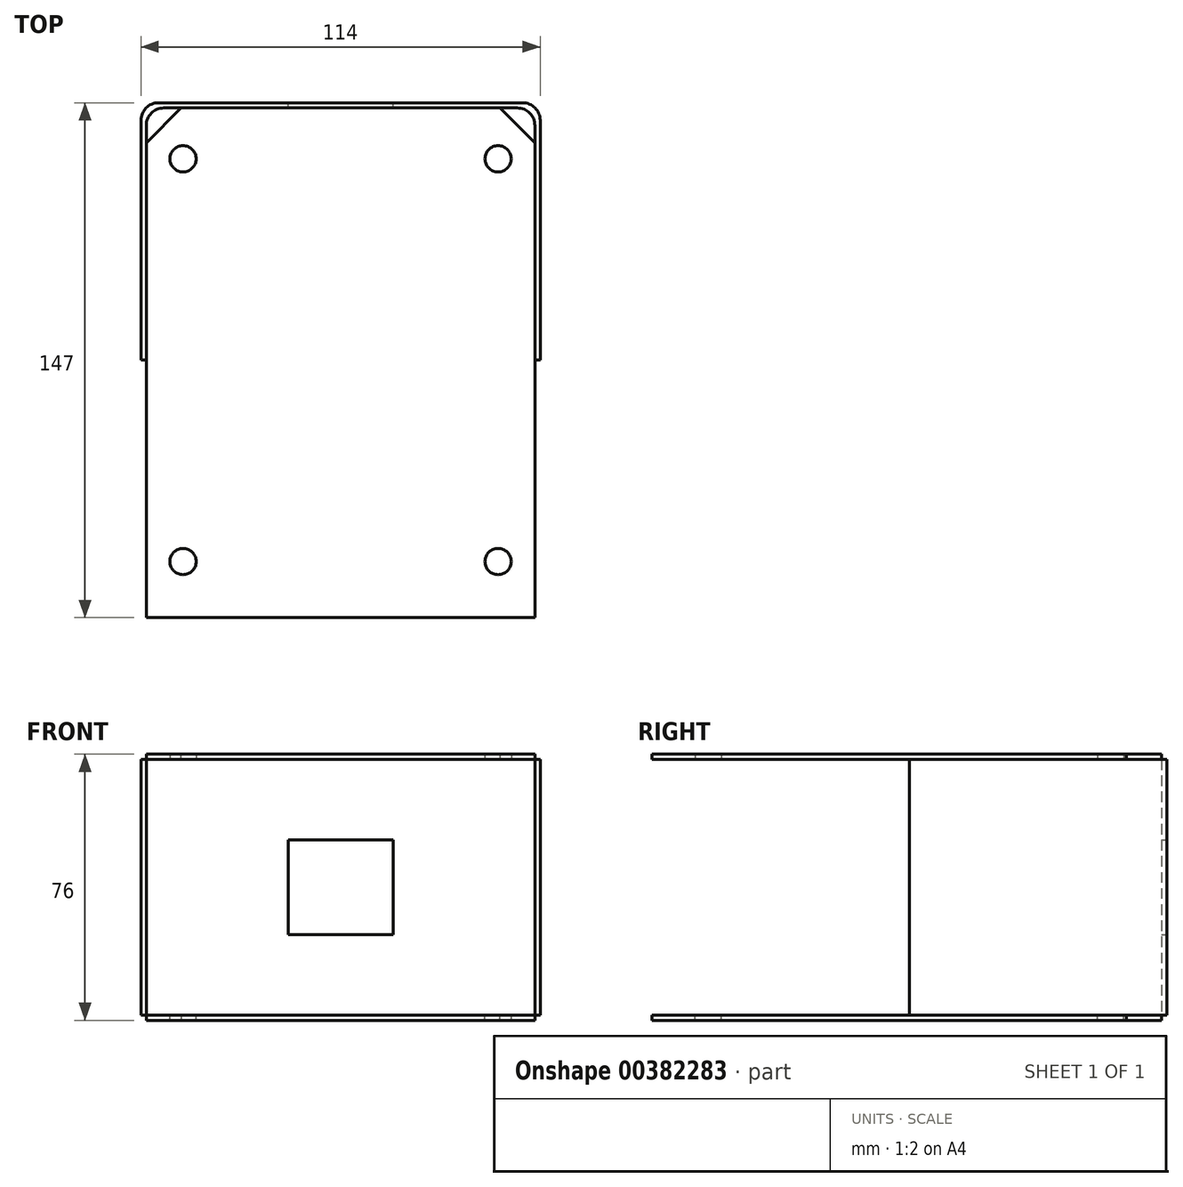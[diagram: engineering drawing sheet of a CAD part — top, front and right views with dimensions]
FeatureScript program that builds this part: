
annotation { "Feature Type Name" : "Feature", "Feature Type Description" : "" }
export const myFeature = defineFeature(function(context is Context, id is Id, definition is map)
    precondition{}
    {
        {
            var Q0;
            Q0=qCreatedBy(makeId("Top.planeOp"),FACE);
            var sketch = newSketch(context, id + "F0", { "sketchPlane" : qUnion([Q0])});
            skLineSegment(sketch, "E0.bottom", {"start": v(57, -73.5) * mm, "end": v(-57, -73.5) * mm});
            skLineSegment(sketch, "E0.top", {"start": v(57, 73.5) * mm, "end": v(-57, 73.5) * mm});
            skLineSegment(sketch, "E0.left", {"start": v(57, -73.5) * mm, "end": v(57, 73.5) * mm});
            skLineSegment(sketch, "E0.right", {"start": v(-57, -73.5) * mm, "end": v(-57, 73.5) * mm});
            skPoint(sketch, "E0.middle", {"position": v(0, 0) * mm});
            skLineSegment(sketch, "E1.0", {"start": v(55.5, -73.5) * mm, "end": v(55.5, 72) * mm});
            skLineSegment(sketch, "E1.1", {"start": v(55.5, 72) * mm, "end": v(-55.5, 72) * mm});
            skLineSegment(sketch, "E1.2", {"start": v(-55.5, -73.5) * mm, "end": v(-55.5, 72) * mm});
            skLineSegment(sketch, "E2.bottom", {"start": v(-57, -73.5) * mm, "end": v(57, -73.5) * mm});
            skLineSegment(sketch, "E2.top", {"start": v(-57, 0) * mm, "end": v(57, 0) * mm});
            skLineSegment(sketch, "E2.left", {"start": v(-57, -73.5) * mm, "end": v(-57, 0) * mm});
            skLineSegment(sketch, "E2.right", {"start": v(57, -73.5) * mm, "end": v(57, 0) * mm});
            skLineSegment(sketch, "E3.top", {"start": v(-57, -36.75) * mm, "end": v(57, -36.75) * mm});
            skLineSegment(sketch, "E3.left", {"start": v(-57, -73.5) * mm, "end": v(-57, -36.75) * mm});
            skLineSegment(sketch, "E3.right", {"start": v(57, -73.5) * mm, "end": v(57, -36.75) * mm});
            skSolve(sketch);
        }
        {
            var Q0;
            {var subQ5=sQuery(id+"F0.wireOp",EDGE,"E2.left");Q0=makeQuery(id+"F0.imprint","IMPRINT",FACE,{"disambiguationData":[TD([[makeQuery(id+"F0.imprint","IMPRINT",EDGE,{"derivedFrom":subQ5}),-1.0]])]});}
            var Q1;
            {var subQ5=sQuery(id+"F0.wireOp",EDGE,"E2.right");Q1=makeQuery(id+"F0.imprint","IMPRINT",FACE,{"disambiguationData":[TD([[makeQuery(id+"F0.imprint","IMPRINT",EDGE,{"derivedFrom":subQ5}),1.0]])]});}
            var Q2;
            Q2=makeQuery(id+"F0.imprint","IMPRINT",FACE,{"disambiguationData":[TD([[makeQuery(id+"F0.imprint","IMPRINT",EDGE,{"derivedFrom":sQuery(id+"F0.wireOp",EDGE,"E0.top")}),1.0]])]});
            extrude(context, id + "F1", {"entities" : qUnion([Q0, Q1, Q2]), "endBound" : BoundingType.SYMMETRIC, "depth" : 73 * mm});
        }
        {
            var Q0;
            Q0=makeQuery(id+"F1.opExtrude","SWEPT_EDGE",EDGE,{"disambiguationData":[OSD([sQuery(id+"F0.wireOp",EDGE,"E0.top"),sQuery(id+"F0.wireOp",EDGE,"E0.left")])]});
            var Q1;
            Q1=makeQuery(id+"F1.opExtrude","SWEPT_EDGE",EDGE,{"disambiguationData":[OSD([sQuery(id+"F0.wireOp",EDGE,"E1.0"),sQuery(id+"F0.wireOp",EDGE,"E1.1")])]});
            var Q2;
            Q2=makeQuery(id+"F1.opExtrude","SWEPT_EDGE",EDGE,{"disambiguationData":[OSD([sQuery(id+"F0.wireOp",EDGE,"E1.1"),sQuery(id+"F0.wireOp",EDGE,"E1.2")])]});
            var Q3;
            Q3=makeQuery(id+"F1.opExtrude","SWEPT_EDGE",EDGE,{"disambiguationData":[OSD([sQuery(id+"F0.wireOp",EDGE,"E0.top"),sQuery(id+"F0.wireOp",EDGE,"E0.right")])]});
            fillet(context, id + "F2", {"entities" : qUnion([Q0, Q1, Q2, Q3]), "radius" : 5 * mm, "tangentPropagation" : true, "allowEdgeOverflow" : false});
        }
        {
            var Q0;
            Q0=makeQuery(id+"F1.opExtrude","CAP_FACE",FACE,{"disambiguationData":[OSD([sQuery(id+"F0.wireOp",EDGE,"E0.top"),sQuery(id+"F0.wireOp",EDGE,"E0.left"),sQuery(id+"F0.wireOp",EDGE,"E0.right"),sQuery(id+"F0.wireOp",EDGE,"E1.0"),sQuery(id+"F0.wireOp",EDGE,"E1.1"),sQuery(id+"F0.wireOp",EDGE,"E1.2"),sQuery(id+"F0.wireOp",EDGE,"E2.left"),sQuery(id+"F0.wireOp",EDGE,"E2.right"),sQuery(id+"F0.wireOp",EDGE,"E3.top")])],"isStart":false});
            var sketch = newSketch(context, id + "F3", { "sketchPlane" : qUnion([Q0])});
            skLineSegment(sketch, "E4.bottom", {"start": v(-57, -73.5) * mm, "end": v(57, -73.5) * mm});
            skLineSegment(sketch, "E4.top", {"start": v(-57, 73.5) * mm, "end": v(57, 73.5) * mm});
            skLineSegment(sketch, "E4.left", {"start": v(-57, -73.5) * mm, "end": v(-57, 73.5) * mm});
            skLineSegment(sketch, "E4.right", {"start": v(57, -73.5) * mm, "end": v(57, 73.5) * mm});
            skPoint(sketch, "E4.middle", {"position": v(0, 0) * mm});
            skLineSegment(sketch, "E5.0", {"start": v(55.5, -73.5) * mm, "end": v(55.5, 72) * mm});
            skLineSegment(sketch, "E5.1", {"start": v(-55.5, 72) * mm, "end": v(55.5, 72) * mm});
            skLineSegment(sketch, "E5.2", {"start": v(-55.5, -73.5) * mm, "end": v(-55.5, 72) * mm});
            skLineSegment(sketch, "E6.bottom", {"start": v(45, -57.5) * mm, "end": v(-45, -57.5) * mm});
            skLineSegment(sketch, "E6.top", {"start": v(45, 57.5) * mm, "end": v(-45, 57.5) * mm});
            skLineSegment(sketch, "E6.left", {"start": v(45, -57.5) * mm, "end": v(45, 57.5) * mm});
            skLineSegment(sketch, "E6.right", {"start": v(-45, -57.5) * mm, "end": v(-45, 57.5) * mm});
            skCircle(sketch, "E7", {"center": v(-45, 57.5) * mm, "radius": 3.75 * mm});
            skCircle(sketch, "E8", {"center": v(45, 57.5) * mm, "radius": 3.75 * mm});
            skCircle(sketch, "E9", {"center": v(45, -57.5) * mm, "radius": 3.75 * mm});
            skCircle(sketch, "E10", {"center": v(-45, -57.5) * mm, "radius": 3.75 * mm});
            skSolve(sketch);
        }
        {
            var Q0;
            {var subQ5=sQuery(id+"F3.wireOp",EDGE,"E9");var subQ10=sQuery(id+"F3.wireOp",EDGE,"E6.bottom");var subQ15=makeQuery(id+"F3.imprint","INTERSECT",VERTEX,{"derivedFrom":[subQ10,subQ5]});Q0=makeQuery(id+"F3.imprint","IMPRINT",FACE,{"disambiguationData":[TD([[makeQuery(id+"F3.imprint","IMPRINT",EDGE,{"disambiguationData":[TD([[subQ15,-1.0]])],"derivedFrom":subQ10}),-1.0]])]});}
            var Q1;
            {var subQ27=sQuery(id+"F3.wireOp",EDGE,"E4.bottom");var subQ30=sQuery(id+"F3.wireOp",EDGE,"E5.0");var subQ31=makeQuery(id+"F3.imprint","INTERSECT",VERTEX,{"derivedFrom":[subQ27,subQ30]});Q1=makeQuery(id+"F3.imprint","IMPRINT",FACE,{"disambiguationData":[TD([[makeQuery(id+"F3.imprint","IMPRINT",EDGE,{"disambiguationData":[TD([[subQ31,1.0]])],"derivedFrom":subQ27}),1.0]])]});}
            var Q2;
            {var subQ1=sQuery(id+"F0.wireOp",EDGE,"E1.2");var subQ2=sQuery(id+"F0.wireOp",EDGE,"E1.1");var subQ3=makeQuery(id+"F2.opFillet","BLEND_EDGE",EDGE,{"blendedFrom":[makeQuery(id+"F1.opExtrude","SWEPT_EDGE",EDGE,{"disambiguationData":[OSD([subQ2,subQ1])]}),makeQuery(id+"F1.opExtrude","CAP_FACE",FACE,{"disambiguationData":[OSD([sQuery(id+"F0.wireOp",EDGE,"E0.top"),sQuery(id+"F0.wireOp",EDGE,"E0.left"),sQuery(id+"F0.wireOp",EDGE,"E0.right"),sQuery(id+"F0.wireOp",EDGE,"E1.0"),subQ2,subQ1,sQuery(id+"F0.wireOp",EDGE,"E2.left"),sQuery(id+"F0.wireOp",EDGE,"E2.right"),sQuery(id+"F0.wireOp",EDGE,"E3.top")])],"isStart":false})],"blendedInto":[makeQuery(id+"F1.opExtrude","CAP_FACE",FACE,{"disambiguationData":[OSD([sQuery(id+"F0.wireOp",EDGE,"E0.top"),sQuery(id+"F0.wireOp",EDGE,"E0.left"),sQuery(id+"F0.wireOp",EDGE,"E0.right"),sQuery(id+"F0.wireOp",EDGE,"E1.0"),subQ2,subQ1,sQuery(id+"F0.wireOp",EDGE,"E2.left"),sQuery(id+"F0.wireOp",EDGE,"E2.right"),sQuery(id+"F0.wireOp",EDGE,"E3.top")])],"isStart":false})]});Q2=makeQuery(id+"F3.imprint","IMPRINT",FACE,{"disambiguationData":[TD([[makeQuery(id+"F3.imprint","IMPRINT",EDGE,{"derivedFrom":subQ3}),1.0]])]});}
            var Q3;
            {var subQ1=sQuery(id+"F0.wireOp",EDGE,"E1.1");var subQ2=sQuery(id+"F0.wireOp",EDGE,"E1.0");var subQ3=makeQuery(id+"F2.opFillet","BLEND_EDGE",EDGE,{"blendedFrom":[makeQuery(id+"F1.opExtrude","SWEPT_EDGE",EDGE,{"disambiguationData":[OSD([subQ2,subQ1])]}),makeQuery(id+"F1.opExtrude","CAP_FACE",FACE,{"disambiguationData":[OSD([sQuery(id+"F0.wireOp",EDGE,"E0.top"),sQuery(id+"F0.wireOp",EDGE,"E0.left"),sQuery(id+"F0.wireOp",EDGE,"E0.right"),subQ2,subQ1,sQuery(id+"F0.wireOp",EDGE,"E1.2"),sQuery(id+"F0.wireOp",EDGE,"E2.left"),sQuery(id+"F0.wireOp",EDGE,"E2.right"),sQuery(id+"F0.wireOp",EDGE,"E3.top")])],"isStart":false})],"blendedInto":[makeQuery(id+"F1.opExtrude","CAP_FACE",FACE,{"disambiguationData":[OSD([sQuery(id+"F0.wireOp",EDGE,"E0.top"),sQuery(id+"F0.wireOp",EDGE,"E0.left"),sQuery(id+"F0.wireOp",EDGE,"E0.right"),subQ2,subQ1,sQuery(id+"F0.wireOp",EDGE,"E1.2"),sQuery(id+"F0.wireOp",EDGE,"E2.left"),sQuery(id+"F0.wireOp",EDGE,"E2.right"),sQuery(id+"F0.wireOp",EDGE,"E3.top")])],"isStart":false})]});Q3=makeQuery(id+"F3.imprint","IMPRINT",FACE,{"disambiguationData":[TD([[makeQuery(id+"F3.imprint","IMPRINT",EDGE,{"derivedFrom":subQ3}),1.0]])]});}
            extrude(context, id + "F4", {"entities" : qUnion([Q0, Q1, Q2, Q3]), "depth" : 1.5 * mm});
        }
        {
            var Q0;
            Q0=makeQuery(id+"F4.opExtrude","SWEPT_EDGE",EDGE,{"disambiguationData":[OSD([sQuery(id+"F3.wireOp",EDGE,"E5.0"),sQuery(id+"F3.wireOp",EDGE,"E5.1")])]});
            var Q1;
            Q1=makeQuery(id+"F4.opExtrude","SWEPT_EDGE",EDGE,{"disambiguationData":[OSD([sQuery(id+"F3.wireOp",EDGE,"E5.1"),sQuery(id+"F3.wireOp",EDGE,"E5.2")])]});
            chamfer(context, id + "F5", {"entities" : qUnion([Q0, Q1]), "width" : 10 * mm, "tangentPropagation" : true});
        }
        {
            var Q0;
            Q0=makeQuery(id+"F4.opExtrude","SWEPT_BODY",BODY,{"disambiguationData":[OSD([sQuery(id+"F3.wireOp",EDGE,"E4.bottom"),sQuery(id+"F3.wireOp",EDGE,"E5.0"),sQuery(id+"F3.wireOp",EDGE,"E5.1"),sQuery(id+"F3.wireOp",EDGE,"E5.2"),sQuery(id+"F3.wireOp",EDGE,"E7"),sQuery(id+"F3.wireOp",EDGE,"E8"),sQuery(id+"F3.wireOp",EDGE,"E9"),sQuery(id+"F3.wireOp",EDGE,"E10")])]});
            var Q1;
            Q1=qCreatedBy(makeId("Top.planeOp"),FACE);
            mirror(context, id + "F6", {"entities" : qUnion([Q0]), "mirrorPlane" : qUnion([Q1])});
        }
        {
            var Q0;
            Q0=makeQuery(id+"F1.opExtrude","SWEPT_FACE",FACE,{"disambiguationData":[OSD([sQuery(id+"F0.wireOp",EDGE,"E0.top")])]});
            var sketch = newSketch(context, id + "F7", { "sketchPlane" : qUnion([Q0])});
            skLineSegment(sketch, "E11.bottom", {"start": v(15, -13.5) * mm, "end": v(-15, -13.5) * mm});
            skLineSegment(sketch, "E11.top", {"start": v(15, 13.5) * mm, "end": v(-15, 13.5) * mm});
            skLineSegment(sketch, "E11.left", {"start": v(15, -13.5) * mm, "end": v(15, 13.5) * mm});
            skLineSegment(sketch, "E11.right", {"start": v(-15, -13.5) * mm, "end": v(-15, 13.5) * mm});
            skPoint(sketch, "E11.middle", {"position": v(0, 0) * mm});
            skSolve(sketch);
        }
        {
            var Q0;
            Q0 = qSketchRegion(id + "F7", true);
            extrude(context, id + "F8", {"entities" : qUnion([Q0]), "operationType" : NewBodyOperationType.REMOVE, "oppositeDirection" : true, "depth" : 12.7 * mm});
        }
    });
